# Revit family: FP_Revit_18_OR36SDI6X1_Range_90001023A
name_source: partatom
category: Specialty Equipment
revit_build: Autodesk Revit 2018 (Build: 20170223_1515(x64)
units: mm (PartAtom-declared; Revit-internal decimal feet)

## family parameters
Always vertical = Yes
Cut with Voids When Loaded = Yes
OmniClass Number = 23.40.40.14.17.17
OmniClass Title = Ranges
Part Type = Normal
Room Calculation Point = No
Round Connector Dimension = Use Diameter
Shared = No
Work Plane-Based = No

## types (1)
- FP_Revit_18_OR36SDI6X1_Range_90001023A
    Cavity - Depth = 641 mm  [stored 2.10302 ft]
    Cavity - Height = 0 mm  [stored 0 ft]
    Cavity - Width = 914 mm  [stored 2.99869 ft]
    Chassis - Depth = 639 mm  [stored 2.09646 ft]
    Chassis - Height = 814 mm
    Chassis - Width = 911 mm  [stored 2.98885 ft]
    Clearance - Overhead Combustible = 762 mm  [stored 2.5 ft]
    Clearance - Overhead Non-Combustible = 610 mm  [stored 2.00131 ft]
    Clearance - Overhead Rangehood = 610 mm  [stored 2.00131 ft]
    Clearance - Rear Combustible = 50 mm  [stored 0.164042 ft]
    Clearance - Rear Non-Combustible = 0 mm  [stored 0 ft]
    Clearance - Side Combustible = 50 mm  [stored 0.164042 ft]
    Clearance - Side Non-Combustible = 0 mm  [stored 0 ft]
    Connector Description - Electrical = 120/208 V or 120/240 V, 60 Hz, 40 A, *NEC Calculated load (50 A, Fused electrical supply)
    Countertop Height (min 908mm - max 933mm) = 915 mm  [stored 3.00197 ft]
    Description = 36" Contemporary Freestanding Induction Range (Stainless)
    Manufacturer = Fisher & Paykel Appliances
    Material - Body = Fisher & Paykel - Stainless Steel
    Material - Buttons and Dials = Fisher & Paykel - Aluminium
    Material - Cooktop = Fisher & Paykel - Black, Matte
    Material - Door Front = Fisher & Paykel - Stainless Steel
    Material - Glass = Fisher & Paykel - Glass, Black
    Material - Handle = Fisher & Paykel - Aluminium
    Material - Trim = Fisher & Paykel - Steel, Chrome Plated
    Model = OR36SDI6X1
    Optional - Rear Trim = TKOR366X1
    Optional - Toe Kick Panel = KICKOR36X1
    Product - Depth = 679 mm
    Product - Height = 915 mm  [stored 3.00197 ft]
    Product - Width = 911 mm  [stored 2.98885 ft]
    URL = www.fisherpaykel.com
    Visibility - Adjustable Feet Covers = Yes
    Visibility - Clearance Required = Yes
    Visibility - Rear Trim (Supplied) = Yes
    Visibility - Rear Trim 3"/76mm (Optional) = No
    Visibility - Toe Kick Panel (Optional) = Yes

note: [stored X ft] marks values corroborated as IEEE doubles in the binary element streams (Revit-internal decimal feet)

## geometry (parser evidence)
native form markers: Sweep x13
no freeform markers — native parametric forms only
